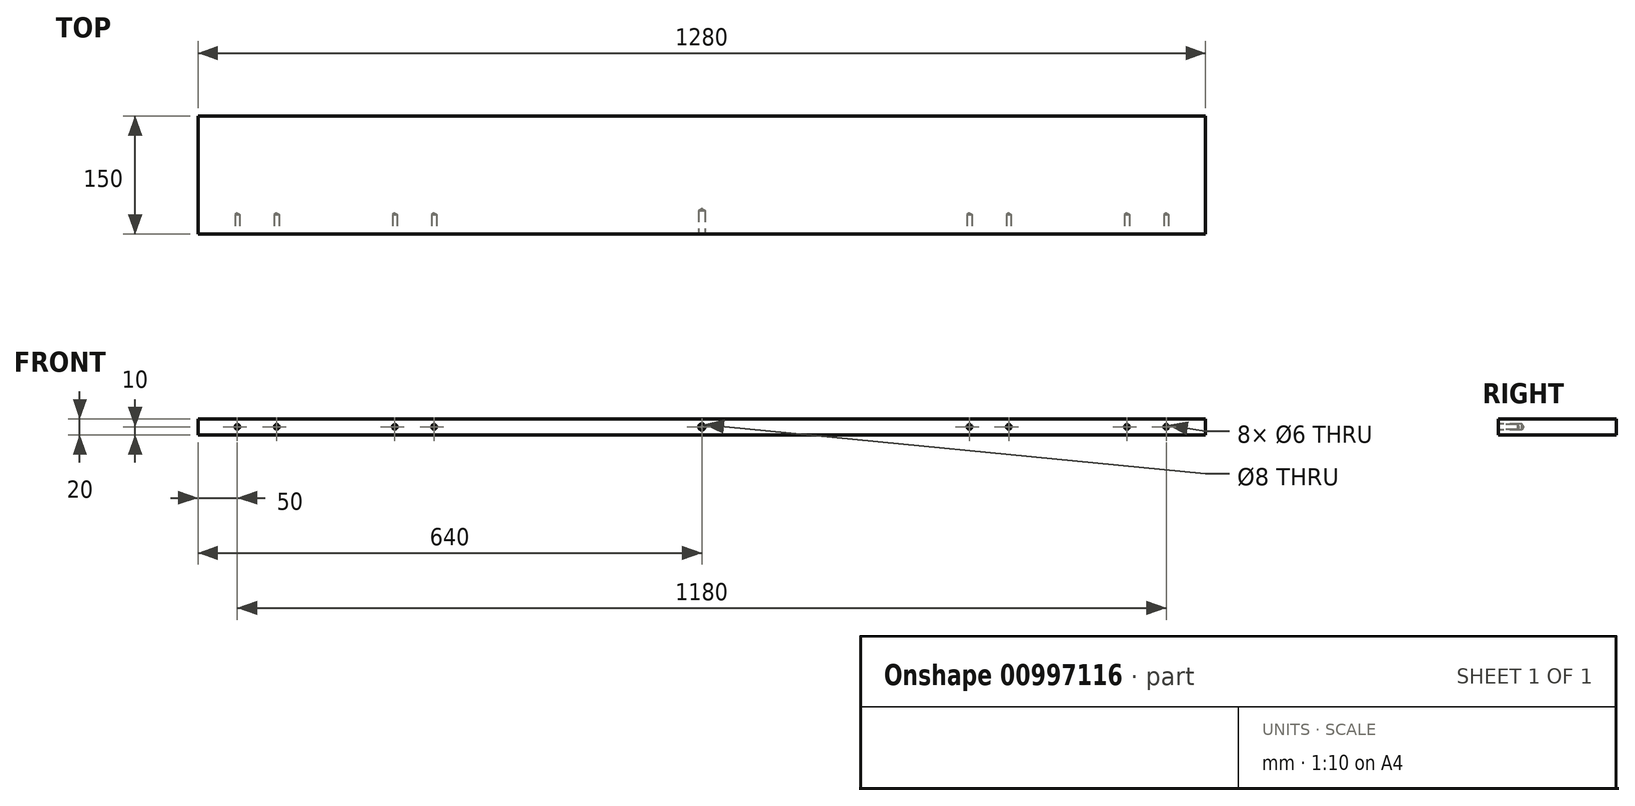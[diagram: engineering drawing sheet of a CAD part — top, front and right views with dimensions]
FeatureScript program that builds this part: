
annotation { "Feature Type Name" : "Feature", "Feature Type Description" : "" }
export const myFeature = defineFeature(function(context is Context, id is Id, definition is map)
    precondition{}
    {
        {
            var Q0;
            Q0=qCreatedBy(makeId("Top.planeOp"),FACE);
            var sketch = newSketch(context, id + "F0", { "sketchPlane" : qUnion([Q0])});
            skLineSegment(sketch, "E0.bottom", {"start": v(640, 75) * mm, "end": v(-640, 75) * mm});
            skLineSegment(sketch, "E0.top", {"start": v(640, -75) * mm, "end": v(-640, -75) * mm});
            skLineSegment(sketch, "E0.left", {"start": v(640, 75) * mm, "end": v(640, -75) * mm});
            skLineSegment(sketch, "E0.right", {"start": v(-640, 75) * mm, "end": v(-640, -75) * mm});
            skPoint(sketch, "E0.middle", {"position": v(0, 0) * mm});
            skSolve(sketch);
        }
        {
            var Q0;
            Q0=qSketchRegion(id+"F0",true);
            extrude(context, id + "F1", {"entities" : qUnion([Q0]), "endBound" : BoundingType.SYMMETRIC, "depth" : 20 * mm, "offsetDistance" : 25 * mm});
        }
        {
            var Q0;
            Q0=makeQuery(id+"F1.opExtrude","SWEPT_FACE",FACE,{"disambiguationData":[OSD([sQuery(id+"F0.wireOp",EDGE,"E0.top")])]});
            var sketch = newSketch(context, id + "F2", { "sketchPlane" : qUnion([Q0])});
            skPoint(sketch, "E1", {"position": v(-590, 0) * mm});
            skPoint(sketch, "E2", {"position": v(-540, 0) * mm});
            skPoint(sketch, "E3", {"position": v(-390, 0) * mm});
            skPoint(sketch, "E4", {"position": v(-340, 0) * mm});
            skPoint(sketch, "E5", {"position": v(590, 0) * mm});
            skPoint(sketch, "E6", {"position": v(540, 0) * mm});
            skPoint(sketch, "E7", {"position": v(390, 0) * mm});
            skPoint(sketch, "E8", {"position": v(340, 0) * mm});
            skPoint(sketch, "E9", {"position": v(0, 0) * mm});
            skSolve(sketch);
        }
        {
            var Q0;
            Q0=sQuery(id+"F2.wireOp",VERTEX,"E1");
            var Q1;
            Q1=sQuery(id+"F2.wireOp",VERTEX,"E2");
            var Q2;
            Q2=sQuery(id+"F2.wireOp",VERTEX,"E3");
            var Q3;
            Q3=sQuery(id+"F2.wireOp",VERTEX,"E4");
            var Q4;
            Q4=sQuery(id+"F2.wireOp",VERTEX,"E8");
            var Q5;
            Q5=sQuery(id+"F2.wireOp",VERTEX,"E7");
            var Q6;
            Q6=sQuery(id+"F2.wireOp",VERTEX,"E6");
            var Q7;
            Q7=sQuery(id+"F2.wireOp",VERTEX,"E5");
            var Q8;
            Q8=makeQuery(id+"F1.opExtrude","SWEPT_BODY",BODY,{"disambiguationData":[OSD([sQuery(id+"F0.wireOp",EDGE,"E0.bottom"),sQuery(id+"F0.wireOp",EDGE,"E0.top"),sQuery(id+"F0.wireOp",EDGE,"E0.left"),sQuery(id+"F0.wireOp",EDGE,"E0.right")])]});
            hole(context, id + "F3", {"style" : HoleStyle.SIMPLE, "endStyle" : HoleEndStyle.BLIND, "holeDiameter" : 6 * mm, "majorDiameter" : 5 * mm, "holeDepth" : 25 * mm, "isTappedThrough" : true, "tappedDepth" : 12 * mm, "tapClearance" : 3, "locations" : qUnion([Q0, Q1, Q2, Q3, Q4, Q5, Q6, Q7]), "scope" : qUnion([Q8])});
        }
        {
            var Q0;
            Q0=sQuery(id+"F2.wireOp",VERTEX,"E9");
            var Q1;
            Q1=makeQuery(id+"F1.opExtrude","SWEPT_BODY",BODY,{"disambiguationData":[OSD([sQuery(id+"F0.wireOp",EDGE,"E0.bottom"),sQuery(id+"F0.wireOp",EDGE,"E0.top"),sQuery(id+"F0.wireOp",EDGE,"E0.left"),sQuery(id+"F0.wireOp",EDGE,"E0.right")])]});
            hole(context, id + "F4", {"style" : HoleStyle.SIMPLE, "endStyle" : HoleEndStyle.BLIND, "holeDiameter" : 8 * mm, "majorDiameter" : 5 * mm, "holeDepth" : 30 * mm, "isTappedThrough" : true, "tappedDepth" : 12 * mm, "tapClearance" : 3, "locations" : qUnion([Q0]), "scope" : qUnion([Q1])});
        }
    });
